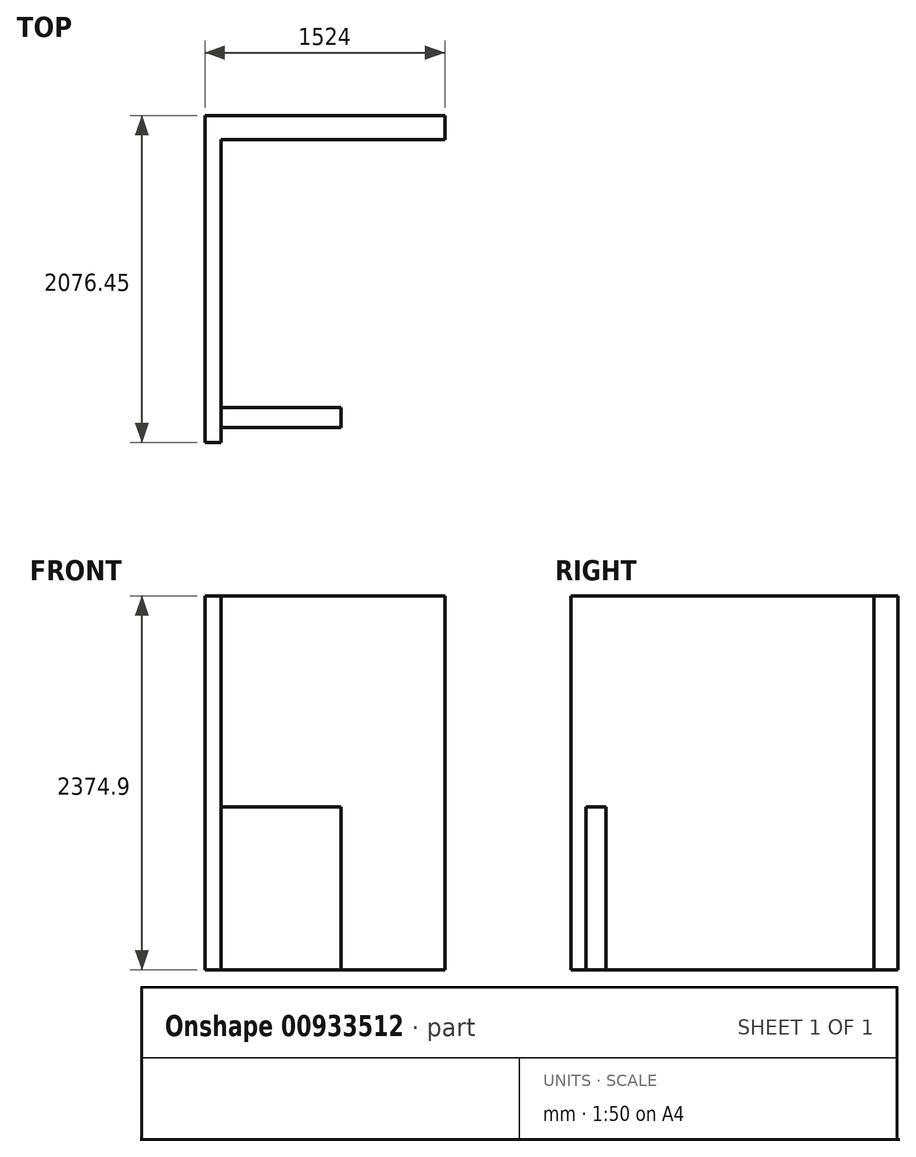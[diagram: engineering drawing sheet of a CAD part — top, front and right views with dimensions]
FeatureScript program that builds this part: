
annotation { "Feature Type Name" : "Feature", "Feature Type Description" : "" }
export const myFeature = defineFeature(function(context is Context, id is Id, definition is map)
    precondition{}
    {
        {
            var Q0;
            Q0=qCreatedBy(makeId("Top.planeOp"),FACE);
            var sketch = newSketch(context, id + "F0", { "sketchPlane" : qUnion([Q0])});
            skLineSegment(sketch, "E0.bottom", {"start": v(0, 0) * mm, "end": v(101.6, 0) * mm});
            skLineSegment(sketch, "E0.top", {"start": v(0, -1924.05) * mm, "end": v(101.6, -1924.05) * mm});
            skLineSegment(sketch, "E0.left", {"start": v(0, 0) * mm, "end": v(0, -1924.05) * mm});
            skLineSegment(sketch, "E0.right", {"start": v(101.6, 0) * mm, "end": v(101.6, -1924.05) * mm});
            skSolve(sketch);
        }
        {
            var Q0;
            Q0=qCreatedBy(makeId("Top.planeOp"),FACE);
            var sketch = newSketch(context, id + "F1", { "sketchPlane" : qUnion([Q0])});
            skLineSegment(sketch, "E1.bottom", {"start": v(0, 0) * mm, "end": v(1524, 0) * mm});
            skLineSegment(sketch, "E1.top", {"start": v(0, 152.4) * mm, "end": v(1524, 152.4) * mm});
            skLineSegment(sketch, "E1.left", {"start": v(0, 0) * mm, "end": v(0, 152.4) * mm});
            skLineSegment(sketch, "E1.right", {"start": v(1524, 0) * mm, "end": v(1524, 152.4) * mm});
            skSolve(sketch);
        }
        {
            var Q0;
            Q0=qCreatedBy(makeId("Top.planeOp"),FACE);
            var sketch = newSketch(context, id + "F2", { "sketchPlane" : qUnion([Q0])});
            skLineSegment(sketch, "E2.bottom", {"start": v(101.6, -1828.8) * mm, "end": v(863.6, -1828.8) * mm});
            skLineSegment(sketch, "E2.top", {"start": v(101.6, -1701.8) * mm, "end": v(863.6, -1701.8) * mm});
            skLineSegment(sketch, "E2.left", {"start": v(101.6, -1828.8) * mm, "end": v(101.6, -1701.8) * mm});
            skLineSegment(sketch, "E2.right", {"start": v(863.6, -1828.8) * mm, "end": v(863.6, -1701.8) * mm});
            skSolve(sketch);
        }
        {
            var Q0;
            Q0 = qSketchRegion(id + "F0", true);
            extrude(context, id + "F3", {"entities" : qUnion([Q0]), "depth" : 2374.9 * mm, "offsetDistance" : 25.4 * mm});
        }
        {
            var Q0;
            Q0 = qSketchRegion(id + "F1", true);
            extrude(context, id + "F4", {"entities" : qUnion([Q0]), "operationType" : NewBodyOperationType.ADD, "depth" : 2374.9 * mm, "offsetDistance" : 25.4 * mm});
        }
        {
            var Q0;
            Q0 = qSketchRegion(id + "F2", true);
            extrude(context, id + "F5", {"entities" : qUnion([Q0]), "operationType" : NewBodyOperationType.ADD, "depth" : 1035.05 * mm, "offsetDistance" : 25.4 * mm});
        }
    });
